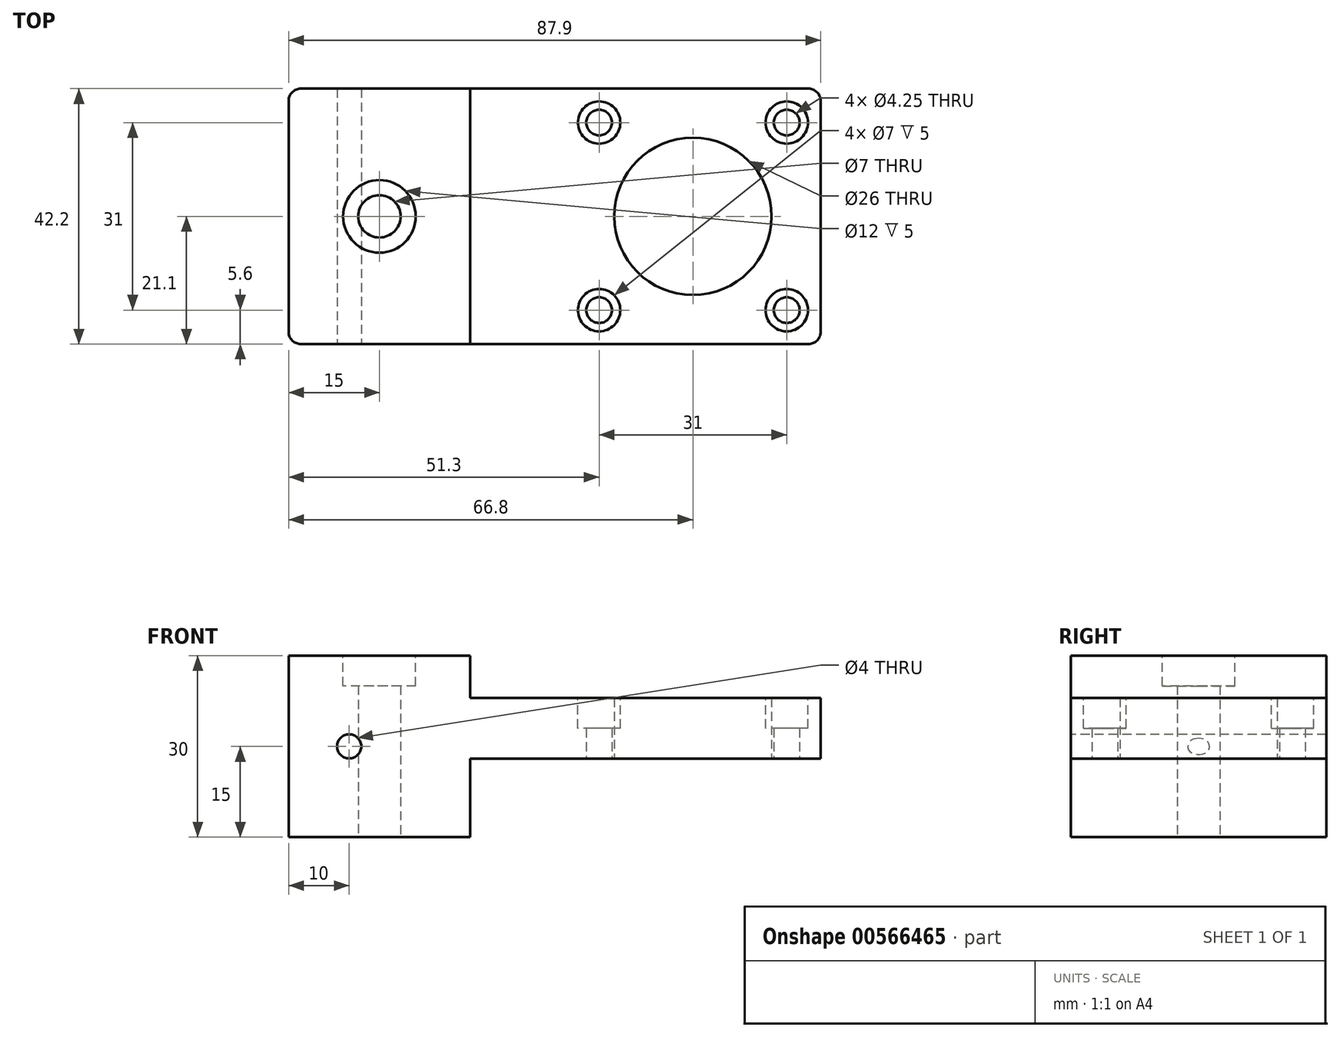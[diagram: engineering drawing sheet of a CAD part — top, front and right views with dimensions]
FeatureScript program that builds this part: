
annotation { "Feature Type Name" : "Feature", "Feature Type Description" : "" }
export const myFeature = defineFeature(function(context is Context, id is Id, definition is map)
    precondition{}
    {
        {
            var Q0;
            Q0=qCreatedBy(makeId("Top.planeOp"),FACE);
            var sketch = newSketch(context, id + "F0", { "sketchPlane" : qUnion([Q0])});
            skCircle(sketch, "E0", {"center": v(0, 0) * mm, "radius": 13 * mm});
            skLineSegment(sketch, "E1.bottom", {"start": v(15.5, -15.5) * mm, "end": v(-15.5, -15.5) * mm, "construction": true});
            skLineSegment(sketch, "E1.top", {"start": v(15.5, 15.5) * mm, "end": v(-15.5, 15.5) * mm, "construction": true});
            skLineSegment(sketch, "E1.left", {"start": v(15.5, -15.5) * mm, "end": v(15.5, 15.5) * mm, "construction": true});
            skLineSegment(sketch, "E1.right", {"start": v(-15.5, -15.5) * mm, "end": v(-15.5, 15.5) * mm, "construction": true});
            skCircle(sketch, "E2", {"center": v(-15.5, 15.5) * mm, "radius": 2.12 * mm});
            skCircle(sketch, "E3", {"center": v(15.5, 15.5) * mm, "radius": 2.12 * mm});
            skCircle(sketch, "E4", {"center": v(15.5, -15.5) * mm, "radius": 2.12 * mm});
            skCircle(sketch, "E5", {"center": v(-15.5, -15.5) * mm, "radius": 2.12 * mm});
            skCircle(sketch, "E6", {"center": v(-51.8, 0) * mm, "radius": 3.5 * mm});
            skCircle(sketch, "E7", {"center": v(0, 0) * mm, "radius": 12.7 * mm, "construction": true});
            skCircle(sketch, "E8", {"center": v(-51.8, 0) * mm, "radius": 38.1 * mm, "construction": true});
            skLineSegment(sketch, "E9", {"start": v(0, 21.1) * mm, "end": v(21.1, 21.1) * mm});
            skLineSegment(sketch, "E10", {"start": v(21.1, 21.1) * mm, "end": v(21.1, 0) * mm});
            skLineSegment(sketch, "E11.MirrorCS", {"start": v(21.1, -21.1) * mm, "end": v(21.1, 0) * mm});
            skLineSegment(sketch, "E12.MirrorCS", {"start": v(0, -21.1) * mm, "end": v(21.1, -21.1) * mm});
            skLineSegment(sketch, "E13.MirrorCS", {"start": v(0, 21.1) * mm, "end": v(-21.1, 21.1) * mm});
            skLineSegment(sketch, "E14.MirrorCS", {"start": v(0, -21.1) * mm, "end": v(-21.1, -21.1) * mm});
            skLineSegment(sketch, "E15", {"start": v(-21.1, 21.1) * mm, "end": v(-66.8, 21.1) * mm});
            skLineSegment(sketch, "E16", {"start": v(-66.8, 21.1) * mm, "end": v(-66.8, 0) * mm});
            skLineSegment(sketch, "E17.MirrorCS", {"start": v(-66.8, -21.1) * mm, "end": v(-66.8, 0) * mm});
            skLineSegment(sketch, "E18.MirrorCS", {"start": v(-21.1, -21.1) * mm, "end": v(-66.8, -21.1) * mm});
            skCircle(sketch, "E19", {"center": v(-51.8, 0) * mm, "radius": 3.5 * mm, "construction": true});
            skCircle(sketch, "E20", {"center": v(-58.5, 0) * mm, "radius": 2 * mm, "construction": true});
            skCircle(sketch, "E21", {"center": v(-41.6, 0) * mm, "radius": 5.5 * mm, "construction": true});
            skSolve(sketch);
        }
        {
            var Q0;
            Q0=qSketchRegion(id+"F0",true);
            extrude(context, id + "F1", {"entities" : qUnion([Q0]), "depth" : 10 * mm});
        }
        {
            var Q0;
            Q0=makeQuery(id+"F1.opExtrude","CAP_FACE",FACE,{"disambiguationData":[OSD([sQuery(id+"F0.wireOp",EDGE,"E0"),sQuery(id+"F0.wireOp",EDGE,"E2"),sQuery(id+"F0.wireOp",EDGE,"E3"),sQuery(id+"F0.wireOp",EDGE,"E4"),sQuery(id+"F0.wireOp",EDGE,"E5"),sQuery(id+"F0.wireOp",EDGE,"E6"),sQuery(id+"F0.wireOp",EDGE,"E9"),sQuery(id+"F0.wireOp",EDGE,"E10"),sQuery(id+"F0.wireOp",EDGE,"E11.MirrorCS"),sQuery(id+"F0.wireOp",EDGE,"E12.MirrorCS"),sQuery(id+"F0.wireOp",EDGE,"E13.MirrorCS"),sQuery(id+"F0.wireOp",EDGE,"E14.MirrorCS"),sQuery(id+"F0.wireOp",EDGE,"E15"),sQuery(id+"F0.wireOp",EDGE,"E16"),sQuery(id+"F0.wireOp",EDGE,"E17.MirrorCS"),sQuery(id+"F0.wireOp",EDGE,"E18.MirrorCS")])],"isStart":false});
            var sketch = newSketch(context, id + "F2", { "sketchPlane" : qUnion([Q0])});
            skCircle(sketch, "E22", {"center": v(-51.8, 0) * mm, "radius": 3.5 * mm});
            skLineSegment(sketch, "E23.bottom", {"start": v(-66.8, 21.1) * mm, "end": v(-36.8, 21.1) * mm});
            skLineSegment(sketch, "E23.top", {"start": v(-66.8, -21.1) * mm, "end": v(-36.8, -21.1) * mm});
            skLineSegment(sketch, "E23.left", {"start": v(-66.8, 21.1) * mm, "end": v(-66.8, -21.1) * mm});
            skLineSegment(sketch, "E23.right", {"start": v(-36.8, 21.1) * mm, "end": v(-36.8, -21.1) * mm});
            skSolve(sketch);
        }
        {
            var Q0;
            Q0=qSketchRegion(id+"F2",true);
            extrude(context, id + "F3", {"entities" : qUnion([Q0]), "operationType" : NewBodyOperationType.ADD, "depth" : 7 * mm});
        }
        {
            var Q0;
            Q0=makeQuery(id+"F1.opExtrude","CAP_FACE",FACE,{"disambiguationData":[OSD([sQuery(id+"F0.wireOp",EDGE,"E0"),sQuery(id+"F0.wireOp",EDGE,"E2"),sQuery(id+"F0.wireOp",EDGE,"E3"),sQuery(id+"F0.wireOp",EDGE,"E4"),sQuery(id+"F0.wireOp",EDGE,"E5"),sQuery(id+"F0.wireOp",EDGE,"E6"),sQuery(id+"F0.wireOp",EDGE,"E9"),sQuery(id+"F0.wireOp",EDGE,"E10"),sQuery(id+"F0.wireOp",EDGE,"E11.MirrorCS"),sQuery(id+"F0.wireOp",EDGE,"E12.MirrorCS"),sQuery(id+"F0.wireOp",EDGE,"E13.MirrorCS"),sQuery(id+"F0.wireOp",EDGE,"E14.MirrorCS"),sQuery(id+"F0.wireOp",EDGE,"E15"),sQuery(id+"F0.wireOp",EDGE,"E16"),sQuery(id+"F0.wireOp",EDGE,"E17.MirrorCS"),sQuery(id+"F0.wireOp",EDGE,"E18.MirrorCS")])],"isStart":false});
            var sketch = newSketch(context, id + "F4", { "sketchPlane" : qUnion([Q0])});
            skCircle(sketch, "E24", {"center": v(-15.5, 15.5) * mm, "radius": 3.5 * mm});
            skCircle(sketch, "E25", {"center": v(15.5, 15.5) * mm, "radius": 3.5 * mm});
            skCircle(sketch, "E26", {"center": v(15.5, -15.5) * mm, "radius": 3.5 * mm});
            skCircle(sketch, "E27", {"center": v(-15.5, -15.5) * mm, "radius": 3.5 * mm});
            skSolve(sketch);
        }
        {
            var Q0;
            Q0=qSketchRegion(id+"F4",true);
            extrude(context, id + "F5", {"entities" : qUnion([Q0]), "operationType" : NewBodyOperationType.REMOVE, "oppositeDirection" : true, "depth" : 5 * mm});
        }
        {
            var Q0;
            Q0=makeQuery(id+"F3.opExtrude","CAP_FACE",FACE,{"disambiguationData":[OSD([sQuery(id+"F2.wireOp",EDGE,"E22"),sQuery(id+"F2.wireOp",EDGE,"E23.bottom"),sQuery(id+"F2.wireOp",EDGE,"E23.top"),sQuery(id+"F2.wireOp",EDGE,"E23.left"),sQuery(id+"F2.wireOp",EDGE,"E23.right")])],"isStart":false});
            var sketch = newSketch(context, id + "F6", { "sketchPlane" : qUnion([Q0])});
            skCircle(sketch, "E28", {"center": v(-51.8, 0) * mm, "radius": 6 * mm});
            skSolve(sketch);
        }
        {
            var Q0;
            Q0=qSketchRegion(id+"F6",true);
            extrude(context, id + "F7", {"entities" : qUnion([Q0]), "operationType" : NewBodyOperationType.REMOVE, "oppositeDirection" : true, "depth" : 5 * mm});
        }
        {
            var Q0;
            Q0=makeQuery(id+"F1.opExtrude","CAP_FACE",FACE,{"disambiguationData":[OSD([sQuery(id+"F0.wireOp",EDGE,"E0"),sQuery(id+"F0.wireOp",EDGE,"E2"),sQuery(id+"F0.wireOp",EDGE,"E3"),sQuery(id+"F0.wireOp",EDGE,"E4"),sQuery(id+"F0.wireOp",EDGE,"E5"),sQuery(id+"F0.wireOp",EDGE,"E6"),sQuery(id+"F0.wireOp",EDGE,"E9"),sQuery(id+"F0.wireOp",EDGE,"E10"),sQuery(id+"F0.wireOp",EDGE,"E11.MirrorCS"),sQuery(id+"F0.wireOp",EDGE,"E12.MirrorCS"),sQuery(id+"F0.wireOp",EDGE,"E13.MirrorCS"),sQuery(id+"F0.wireOp",EDGE,"E14.MirrorCS"),sQuery(id+"F0.wireOp",EDGE,"E15"),sQuery(id+"F0.wireOp",EDGE,"E16"),sQuery(id+"F0.wireOp",EDGE,"E17.MirrorCS"),sQuery(id+"F0.wireOp",EDGE,"E18.MirrorCS")])],"isStart":true});
            var sketch = newSketch(context, id + "F8", { "sketchPlane" : qUnion([Q0])});
            skLineSegment(sketch, "E29.bottom", {"start": v(-66.8, 21.1) * mm, "end": v(-36.8, 21.1) * mm});
            skLineSegment(sketch, "E29.top", {"start": v(-66.8, -21.1) * mm, "end": v(-36.8, -21.1) * mm});
            skLineSegment(sketch, "E29.left", {"start": v(-66.8, 21.1) * mm, "end": v(-66.8, -21.1) * mm});
            skLineSegment(sketch, "E29.right", {"start": v(-36.8, 21.1) * mm, "end": v(-36.8, -21.1) * mm});
            skCircle(sketch, "E30", {"center": v(-51.8, 0) * mm, "radius": 3.5 * mm});
            skSolve(sketch);
        }
        {
            var Q0;
            Q0=qSketchRegion(id+"F8",true);
            extrude(context, id + "F9", {"entities" : qUnion([Q0]), "operationType" : NewBodyOperationType.ADD, "depth" : 13 * mm});
        }
        {
            var Q0;
            Q0=makeQuery(id+"F9.boolean.opBoolean","MERGE",FACE,{"derivedFrom":[makeQuery(id+"F3.boolean.opBoolean","MERGE",FACE,{"derivedFrom":[makeQuery(id+"F1.opExtrude","SWEPT_FACE",FACE,{"disambiguationData":[OSD([sQuery(id+"F0.wireOp",EDGE,"E12.MirrorCS"),sQuery(id+"F0.wireOp",EDGE,"E14.MirrorCS"),sQuery(id+"F0.wireOp",EDGE,"E18.MirrorCS")])]}),makeQuery(id+"F3.opExtrude","SWEPT_FACE",FACE,{"disambiguationData":[OSD([sQuery(id+"F2.wireOp",EDGE,"E23.top")])]})]}),makeQuery(id+"F9.opExtrude","SWEPT_FACE",FACE,{"disambiguationData":[OSD([sQuery(id+"F8.wireOp",EDGE,"E29.bottom")])]})]});
            var sketch = newSketch(context, id + "F10", { "sketchPlane" : qUnion([Q0])});
            skCircle(sketch, "E31", {"center": v(-56.8, 2) * mm, "radius": 2 * mm});
            skSolve(sketch);
        }
        {
            var Q0;
            Q0=qSketchRegion(id+"F10",true);
            extrude(context, id + "F11", {"entities" : qUnion([Q0]), "operationType" : NewBodyOperationType.REMOVE, "endBound" : BoundingType.THROUGH_ALL, "oppositeDirection" : true, "depth" : 25 * mm});
        }
        {
            var Q0;
            Q0=makeQuery(id+"F1.opExtrude","SWEPT_EDGE",EDGE,{"disambiguationData":[OSD([sQuery(id+"F0.wireOp",EDGE,"E9"),sQuery(id+"F0.wireOp",EDGE,"E10")])]});
            var Q1;
            Q1=makeQuery(id+"F1.opExtrude","SWEPT_EDGE",EDGE,{"disambiguationData":[OSD([sQuery(id+"F0.wireOp",EDGE,"E11.MirrorCS"),sQuery(id+"F0.wireOp",EDGE,"E12.MirrorCS")])]});
            var Q2;
            Q2=makeQuery(id+"F1.opExtrude","SWEPT_EDGE",EDGE,{"disambiguationData":[OSD([sQuery(id+"F0.wireOp",EDGE,"E17.MirrorCS"),sQuery(id+"F0.wireOp",EDGE,"E18.MirrorCS")])]});
            var Q3;
            Q3=makeQuery(id+"F1.opExtrude","SWEPT_EDGE",EDGE,{"disambiguationData":[OSD([sQuery(id+"F0.wireOp",EDGE,"E15"),sQuery(id+"F0.wireOp",EDGE,"E16")])]});
            fillet(context, id + "F12", {"entities" : qUnion([Q0, Q1, Q2, Q3]), "radius" : 2 * mm, "tangentPropagation" : true, "allowEdgeOverflow" : false});
        }
    });
